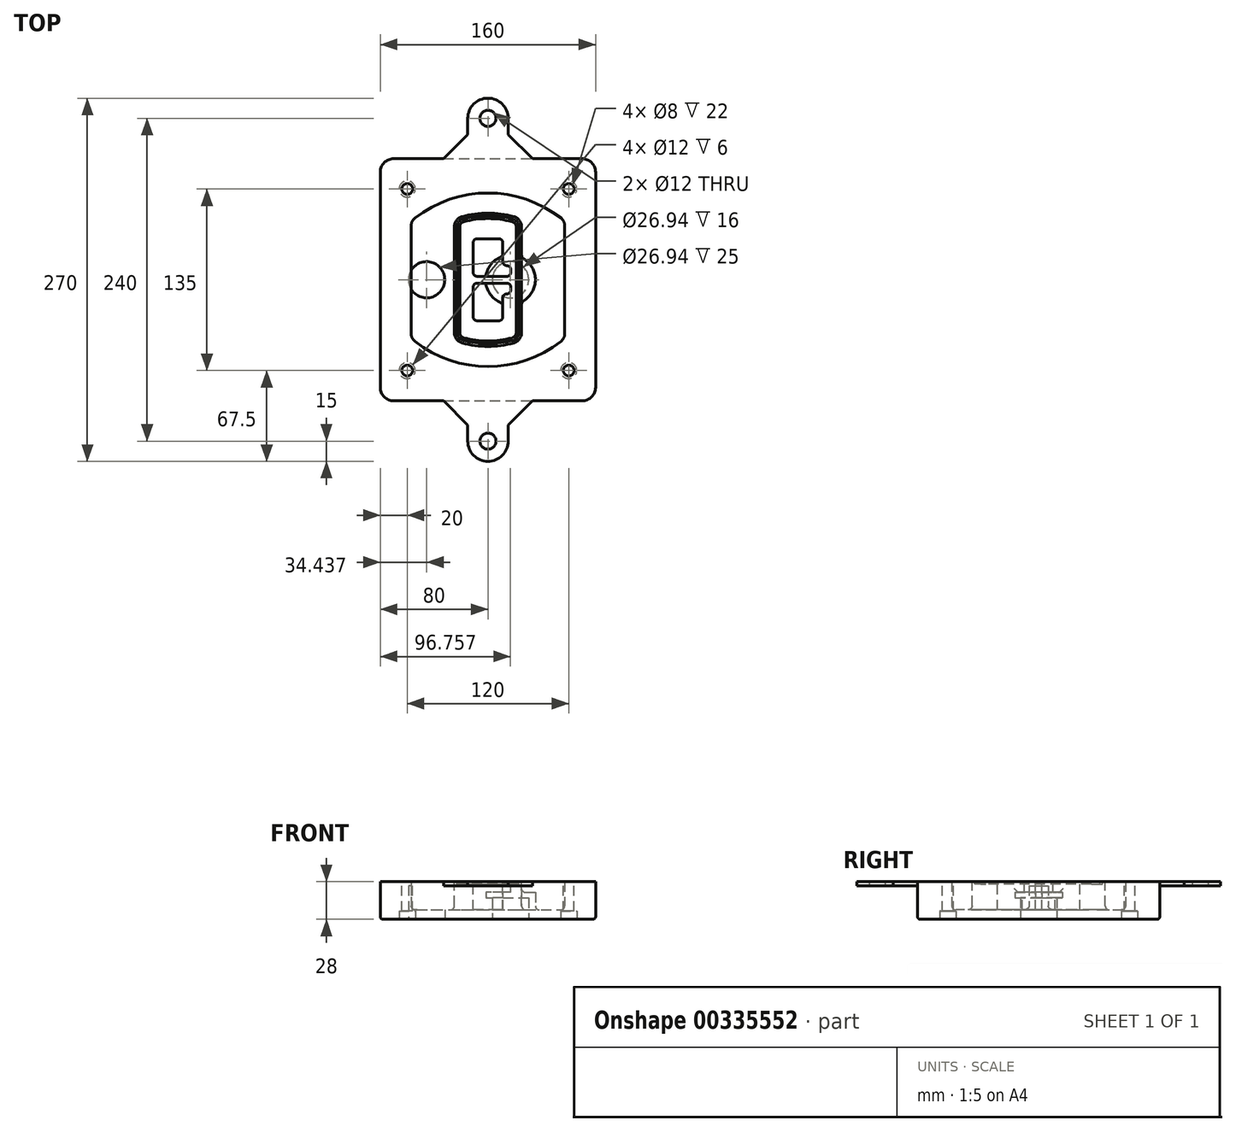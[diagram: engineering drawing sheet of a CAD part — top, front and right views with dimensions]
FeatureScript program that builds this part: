
annotation { "Feature Type Name" : "Feature", "Feature Type Description" : "" }
export const myFeature = defineFeature(function(context is Context, id is Id, definition is map)
    precondition{}
    {
        {
            var Q0;
            Q0=qCreatedBy(makeId("Top.planeOp"),FACE);
            var sketch = newSketch(context, id + "F0", { "sketchPlane" : qUnion([Q0])});
            skPoint(sketch, "E0.rect.middle", {"position": v(0, 0) * mm});
            skLineSegment(sketch, "E1.bottom", {"start": v(-70, -90) * mm, "end": v(70, -90) * mm});
            skLineSegment(sketch, "E1.top", {"start": v(-70, 90) * mm, "end": v(70, 90) * mm});
            skLineSegment(sketch, "E1.left", {"start": v(-80, -80) * mm, "end": v(-80, 80) * mm});
            skLineSegment(sketch, "E1.right", {"start": v(80, -80) * mm, "end": v(80, 80) * mm});
            skLineSegment(sketch, "E2", {"start": v(-80, 90) * mm, "end": v(80, -90) * mm, "construction": true});
            skLineSegment(sketch, "E3", {"start": v(80, 90) * mm, "end": v(-80, -90) * mm, "construction": true});
            skCircle(sketch, "E4", {"center": v(-60, 67.5) * mm, "radius": 4 * mm});
            skCircle(sketch, "E5", {"center": v(60, 67.5) * mm, "radius": 4 * mm});
            skCircle(sketch, "E6", {"center": v(60, -67.5) * mm, "radius": 4 * mm});
            skCircle(sketch, "E7", {"center": v(-60, -67.5) * mm, "radius": 4 * mm});
            skLineSegment(sketch, "E8", {"start": v(-60, 67.5) * mm, "end": v(60, 67.5) * mm, "construction": true});
            skLineSegment(sketch, "E9", {"start": v(60, 67.5) * mm, "end": v(60, -67.5) * mm, "construction": true});
            skLineSegment(sketch, "E10", {"start": v(60, -67.5) * mm, "end": v(-60, -67.5) * mm, "construction": true});
            skLineSegment(sketch, "E11", {"start": v(-60, -67.5) * mm, "end": v(-60, 67.5) * mm, "construction": true});
            skLineSegment(sketch, "E12", {"start": v(-60, 40.3) * mm, "end": v(-60, -40.3) * mm});
            skLineSegment(sketch, "E13", {"start": v(60, 40.3) * mm, "end": v(60, -40.3) * mm});
            skArc(sketch, "E14", {"start": v(56.15, 48.18) * mm, "mid": v(0, 67.5) * mm, "end": v(-56.15, 48.18) * mm});
            skArc(sketch, "E15", {"start": v(-56.15, -48.18) * mm, "mid": v(0, -67.5) * mm, "end": v(56.15, -48.18) * mm});
            skLineSegment(sketch, "E16", {"start": v(-60, 0) * mm, "end": v(60, 0) * mm, "construction": true});
            skPoint(sketch, "E17.visualSharp", {"position": v(-60, -45) * mm});
            skArc(sketch, "E17.filletArc", {"start": v(-60, -40.3) * mm, "mid": v(-58.99, -44.68) * mm, "end": v(-56.15, -48.18) * mm});
            skPoint(sketch, "E18.visualSharp", {"position": v(-60, 45) * mm});
            skArc(sketch, "E18.filletArc", {"start": v(-56.15, 48.18) * mm, "mid": v(-58.99, 44.68) * mm, "end": v(-60, 40.3) * mm});
            skPoint(sketch, "E19.visualSharp", {"position": v(60, 45) * mm});
            skArc(sketch, "E19.filletArc", {"start": v(60, 40.3) * mm, "mid": v(58.99, 44.68) * mm, "end": v(56.15, 48.18) * mm});
            skPoint(sketch, "E20.visualSharp", {"position": v(60, -45) * mm});
            skArc(sketch, "E20.filletArc", {"start": v(56.15, -48.18) * mm, "mid": v(58.99, -44.68) * mm, "end": v(60, -40.3) * mm});
            skPoint(sketch, "E21.visualSharp", {"position": v(-80, 90) * mm});
            skArc(sketch, "E21.filletArc", {"start": v(-70, 90) * mm, "mid": v(-77.07, 87.07) * mm, "end": v(-80, 80) * mm});
            skPoint(sketch, "E22.visualSharp", {"position": v(80, 90) * mm});
            skArc(sketch, "E22.filletArc", {"start": v(80, 80) * mm, "mid": v(77.07, 87.07) * mm, "end": v(70, 90) * mm});
            skPoint(sketch, "E23.visualSharp", {"position": v(80, -90) * mm});
            skArc(sketch, "E23.filletArc", {"start": v(70, -90) * mm, "mid": v(77.07, -87.07) * mm, "end": v(80, -80) * mm});
            skPoint(sketch, "E24.visualSharp", {"position": v(-80, -90) * mm});
            skArc(sketch, "E24.filletArc", {"start": v(-80, -80) * mm, "mid": v(-77.07, -87.07) * mm, "end": v(-70, -90) * mm});
            skArc(sketch, "E25.0", {"start": v(57, 40.3) * mm, "mid": v(56.3, 43.36) * mm, "end": v(54.3, 45.81) * mm});
            skLineSegment(sketch, "E25.1", {"start": v(57, 40.3) * mm, "end": v(57, -40.3) * mm});
            skArc(sketch, "E25.2", {"start": v(54.3, -45.81) * mm, "mid": v(56.3, -43.36) * mm, "end": v(57, -40.3) * mm});
            skArc(sketch, "E25.3", {"start": v(-54.3, -45.81) * mm, "mid": v(0, -64.5) * mm, "end": v(54.3, -45.81) * mm});
            skArc(sketch, "E25.4", {"start": v(-57, -40.3) * mm, "mid": v(-56.3, -43.36) * mm, "end": v(-54.3, -45.81) * mm});
            skArc(sketch, "E25.5", {"start": v(54.3, 45.81) * mm, "mid": v(0, 64.5) * mm, "end": v(-54.3, 45.81) * mm});
            skLineSegment(sketch, "E25.6", {"start": v(-57, 40.3) * mm, "end": v(-57, -40.3) * mm});
            skArc(sketch, "E25.7", {"start": v(-54.3, 45.81) * mm, "mid": v(-56.3, 43.36) * mm, "end": v(-57, 40.3) * mm});
            skArc(sketch, "E26.0", {"start": v(-58.62, 51.33) * mm, "mid": v(-62.58, 46.43) * mm, "end": v(-64, 40.3) * mm});
            skArc(sketch, "E26.1", {"start": v(58.62, 51.33) * mm, "mid": v(0, 71.5) * mm, "end": v(-58.62, 51.33) * mm});
            skArc(sketch, "E26.2", {"start": v(64, 40.3) * mm, "mid": v(62.58, 46.43) * mm, "end": v(58.62, 51.33) * mm});
            skLineSegment(sketch, "E26.3", {"start": v(64, 40.3) * mm, "end": v(64, -40.3) * mm});
            skArc(sketch, "E26.4", {"start": v(58.62, -51.33) * mm, "mid": v(62.58, -46.43) * mm, "end": v(64, -40.3) * mm});
            skLineSegment(sketch, "E26.5", {"start": v(-64, 40.3) * mm, "end": v(-64, -40.3) * mm});
            skArc(sketch, "E26.6", {"start": v(-58.62, -51.33) * mm, "mid": v(0, -71.5) * mm, "end": v(58.62, -51.33) * mm});
            skArc(sketch, "E26.7", {"start": v(-64, -40.3) * mm, "mid": v(-62.58, -46.43) * mm, "end": v(-58.62, -51.33) * mm});
            skSolve(sketch);
        }
        {
            var Q0;
            Q0=makeQuery(id+"F0.imprint","IMPRINT",FACE,{"disambiguationData":[TD([[makeQuery(id+"F0.imprint","IMPRINT",EDGE,{"derivedFrom":sQuery(id+"F0.wireOp",EDGE,"E1.bottom")}),1.0]])]});
            var Q1;
            Q1=makeQuery(id+"F0.imprint","IMPRINT",FACE,{"disambiguationData":[TD([[makeQuery(id+"F0.imprint","IMPRINT",EDGE,{"derivedFrom":sQuery(id+"F0.wireOp",EDGE,"E12")}),1.0]])]});
            var Q2;
            Q2=makeQuery(id+"F0.imprint","IMPRINT",FACE,{"disambiguationData":[TD([[makeQuery(id+"F0.imprint","IMPRINT",EDGE,{"derivedFrom":sQuery(id+"F0.wireOp",EDGE,"E25.0")}),1.0]])]});
            var Q3;
            Q3=makeQuery(id+"F0.imprint","IMPRINT",FACE,{"disambiguationData":[TD([[makeQuery(id+"F0.imprint","IMPRINT",EDGE,{"derivedFrom":sQuery(id+"F0.wireOp",EDGE,"E12")}),-1.0]])]});
            extrude(context, id + "F1", {"entities" : qUnion([Q0, Q1, Q2, Q3]), "oppositeDirection" : true, "depth" : 25 * mm});
        }
        {
            var Q0;
            Q0=makeQuery(id+"F0.imprint","IMPRINT",FACE,{"disambiguationData":[TD([[makeQuery(id+"F0.imprint","IMPRINT",EDGE,{"derivedFrom":sQuery(id+"F0.wireOp",EDGE,"E12")}),1.0]])]});
            extrude(context, id + "F2", {"entities" : qUnion([Q0]), "operationType" : NewBodyOperationType.ADD, "depth" : 3 * mm});
        }
        {
            var Q0;
            Q0=makeQuery(id+"F0.imprint","IMPRINT",FACE,{"disambiguationData":[TD([[makeQuery(id+"F0.imprint","IMPRINT",EDGE,{"derivedFrom":sQuery(id+"F0.wireOp",EDGE,"E25.0")}),1.0]])]});
            extrude(context, id + "F3", {"entities" : qUnion([Q0]), "operationType" : NewBodyOperationType.REMOVE, "oppositeDirection" : true, "depth" : 18 * mm});
        }
        {
            var Q0;
            Q0=makeQuery(id+"F2.opExtrude","CAP_FACE",FACE,{"disambiguationData":[OSD([sQuery(id+"F0.wireOp",EDGE,"E12"),sQuery(id+"F0.wireOp",EDGE,"E13"),sQuery(id+"F0.wireOp",EDGE,"E14"),sQuery(id+"F0.wireOp",EDGE,"E15"),sQuery(id+"F0.wireOp",EDGE,"E17.filletArc"),sQuery(id+"F0.wireOp",EDGE,"E18.filletArc"),sQuery(id+"F0.wireOp",EDGE,"E19.filletArc"),sQuery(id+"F0.wireOp",EDGE,"E20.filletArc"),sQuery(id+"F0.wireOp",EDGE,"E25.0"),sQuery(id+"F0.wireOp",EDGE,"E25.1"),sQuery(id+"F0.wireOp",EDGE,"E25.2"),sQuery(id+"F0.wireOp",EDGE,"E25.3"),sQuery(id+"F0.wireOp",EDGE,"E25.4"),sQuery(id+"F0.wireOp",EDGE,"E25.5"),sQuery(id+"F0.wireOp",EDGE,"E25.6"),sQuery(id+"F0.wireOp",EDGE,"E25.7")])],"isStart":false});
            var sketch = newSketch(context, id + "F4", { "sketchPlane" : qUnion([Q0])});
            skArc(sketch, "E27.0", {"start": v(-19.08, -46.97) * mm, "mid": v(0, -49.5) * mm, "end": v(19.08, -46.97) * mm});
            skArc(sketch, "E28.0", {"start": v(19.08, 46.97) * mm, "mid": v(0, 49.5) * mm, "end": v(-19.08, 46.97) * mm});
            skLineSegment(sketch, "E29", {"start": v(-25, 39.25) * mm, "end": v(-25, -39.25) * mm});
            skLineSegment(sketch, "E30", {"start": v(25, 39.25) * mm, "end": v(25, -39.25) * mm});
            skLineSegment(sketch, "E31", {"start": v(-25, 45.1) * mm, "end": v(25, 45.1) * mm, "construction": true});
            skLineSegment(sketch, "E32", {"start": v(-25, -45.1) * mm, "end": v(25, -45.1) * mm, "construction": true});
            skPoint(sketch, "E33.visualSharp", {"position": v(-25, 45.1) * mm});
            skArc(sketch, "E33.filletArc", {"start": v(-19.08, 46.97) * mm, "mid": v(-23.35, 44.11) * mm, "end": v(-25, 39.25) * mm});
            skPoint(sketch, "E34.visualSharp", {"position": v(25, 45.1) * mm});
            skArc(sketch, "E34.filletArc", {"start": v(25, 39.25) * mm, "mid": v(23.35, 44.11) * mm, "end": v(19.08, 46.97) * mm});
            skPoint(sketch, "E35.visualSharp", {"position": v(25, -45.1) * mm});
            skArc(sketch, "E35.filletArc", {"start": v(19.08, -46.97) * mm, "mid": v(23.35, -44.11) * mm, "end": v(25, -39.25) * mm});
            skPoint(sketch, "E36.visualSharp", {"position": v(-25, -45.1) * mm});
            skArc(sketch, "E36.filletArc", {"start": v(-25, -39.25) * mm, "mid": v(-23.35, -44.11) * mm, "end": v(-19.08, -46.97) * mm});
            skArc(sketch, "E37.0", {"start": v(54.3, 45.81) * mm, "mid": v(0, 64.5) * mm, "end": v(-54.3, 45.81) * mm});
            skArc(sketch, "E37.1", {"start": v(-54.3, 45.81) * mm, "mid": v(-56.3, 43.36) * mm, "end": v(-57, 40.3) * mm});
            skLineSegment(sketch, "E37.2", {"start": v(-57, 40.3) * mm, "end": v(-57, -40.3) * mm});
            skArc(sketch, "E37.3", {"start": v(-57, -40.3) * mm, "mid": v(-56.3, -43.36) * mm, "end": v(-54.3, -45.81) * mm});
            skArc(sketch, "E37.4", {"start": v(-54.3, -45.81) * mm, "mid": v(0, -64.5) * mm, "end": v(54.3, -45.81) * mm});
            skArc(sketch, "E37.5", {"start": v(54.3, -45.81) * mm, "mid": v(56.3, -43.36) * mm, "end": v(57, -40.3) * mm});
            skLineSegment(sketch, "E37.6", {"start": v(57, 40.3) * mm, "end": v(57, -40.3) * mm});
            skArc(sketch, "E37.7", {"start": v(57, 40.3) * mm, "mid": v(56.3, 43.36) * mm, "end": v(54.3, 45.81) * mm});
            skLineSegment(sketch, "E38.0", {"start": v(23, 39.25) * mm, "end": v(23, -39.25) * mm});
            skArc(sketch, "E38.1", {"start": v(18.56, -45.04) * mm, "mid": v(21.76, -42.9) * mm, "end": v(23, -39.25) * mm});
            skArc(sketch, "E38.2", {"start": v(-18.56, -45.04) * mm, "mid": v(0, -47.5) * mm, "end": v(18.56, -45.04) * mm});
            skArc(sketch, "E38.3", {"start": v(-23, -39.25) * mm, "mid": v(-21.76, -42.9) * mm, "end": v(-18.56, -45.04) * mm});
            skLineSegment(sketch, "E38.4", {"start": v(-23, 39.25) * mm, "end": v(-23, -39.25) * mm});
            skArc(sketch, "E38.5", {"start": v(23, 39.25) * mm, "mid": v(21.76, 42.9) * mm, "end": v(18.56, 45.04) * mm});
            skArc(sketch, "E38.6", {"start": v(-18.56, 45.04) * mm, "mid": v(-21.76, 42.9) * mm, "end": v(-23, 39.25) * mm});
            skArc(sketch, "E38.7", {"start": v(18.56, 45.04) * mm, "mid": v(0, 47.5) * mm, "end": v(-18.56, 45.04) * mm});
            skArc(sketch, "E39.0", {"start": v(21, 39.25) * mm, "mid": v(20.18, 41.68) * mm, "end": v(18.04, 43.1) * mm});
            skLineSegment(sketch, "E39.1", {"start": v(21, 39.25) * mm, "end": v(21, -39.25) * mm});
            skArc(sketch, "E39.2", {"start": v(18.04, -43.1) * mm, "mid": v(20.18, -41.68) * mm, "end": v(21, -39.25) * mm});
            skArc(sketch, "E39.3", {"start": v(-18.04, -43.1) * mm, "mid": v(0, -45.5) * mm, "end": v(18.04, -43.1) * mm});
            skArc(sketch, "E39.4", {"start": v(-21, -39.25) * mm, "mid": v(-20.18, -41.68) * mm, "end": v(-18.04, -43.1) * mm});
            skArc(sketch, "E39.5", {"start": v(18.04, 43.1) * mm, "mid": v(0, 45.5) * mm, "end": v(-18.04, 43.1) * mm});
            skLineSegment(sketch, "E39.6", {"start": v(-21, 39.25) * mm, "end": v(-21, -39.25) * mm});
            skArc(sketch, "E39.7", {"start": v(-18.04, 43.1) * mm, "mid": v(-20.18, 41.68) * mm, "end": v(-21, 39.25) * mm});
            skLineSegment(sketch, "E40", {"start": v(-25, 0) * mm, "end": v(25, 0) * mm, "construction": true});
            skLineSegment(sketch, "E41", {"start": v(-11, 5.5) * mm, "end": v(-11, 27.5) * mm});
            skLineSegment(sketch, "E42", {"start": v(-8, 30.5) * mm, "end": v(8, 30.5) * mm});
            skLineSegment(sketch, "E43", {"start": v(11, 27.5) * mm, "end": v(11, 13.5) * mm});
            skLineSegment(sketch, "E44", {"start": v(14, 10.5) * mm, "end": v(14, 10.5) * mm});
            skLineSegment(sketch, "E45", {"start": v(17, 7.5) * mm, "end": v(17, 5.5) * mm});
            skLineSegment(sketch, "E46", {"start": v(14, 2.5) * mm, "end": v(-8, 2.5) * mm});
            skPoint(sketch, "E47.visualSharp", {"position": v(-11, 30.5) * mm});
            skArc(sketch, "E47.filletArc", {"start": v(-8, 30.5) * mm, "mid": v(-10.12, 29.62) * mm, "end": v(-11, 27.5) * mm});
            skPoint(sketch, "E48.visualSharp", {"position": v(11, 30.5) * mm});
            skArc(sketch, "E48.filletArc", {"start": v(11, 27.5) * mm, "mid": v(10.12, 29.62) * mm, "end": v(8, 30.5) * mm});
            skPoint(sketch, "E49.visualSharp", {"position": v(11, 10.5) * mm});
            skArc(sketch, "E49.filletArc", {"start": v(11, 13.5) * mm, "mid": v(11.88, 11.38) * mm, "end": v(14, 10.5) * mm});
            skPoint(sketch, "E50.visualSharp", {"position": v(17, 10.5) * mm});
            skArc(sketch, "E50.filletArc", {"start": v(17, 7.5) * mm, "mid": v(16.12, 9.62) * mm, "end": v(14, 10.5) * mm});
            skPoint(sketch, "E51.visualSharp", {"position": v(17, 2.5) * mm});
            skArc(sketch, "E51.filletArc", {"start": v(14, 2.5) * mm, "mid": v(16.12, 3.38) * mm, "end": v(17, 5.5) * mm});
            skPoint(sketch, "E52.visualSharp", {"position": v(-11, 2.5) * mm});
            skArc(sketch, "E52.filletArc", {"start": v(-11, 5.5) * mm, "mid": v(-10.12, 3.38) * mm, "end": v(-8, 2.5) * mm});
            skLineSegment(sketch, "E53.0.MirrorCS", {"start": v(14, -2.5) * mm, "end": v(-8, -2.5) * mm});
            skArc(sketch, "E54.0.MirrorCS", {"start": v(-11, -5.5) * mm, "mid": v(-10.12, -3.38) * mm, "end": v(-8, -2.5) * mm});
            skLineSegment(sketch, "E55.0.MirrorCS", {"start": v(-11, -5.5) * mm, "end": v(-11, -27.5) * mm});
            skArc(sketch, "E56.0.MirrorCS", {"start": v(-8, -30.5) * mm, "mid": v(-10.12, -29.62) * mm, "end": v(-11, -27.5) * mm});
            skLineSegment(sketch, "E57.0.MirrorCS", {"start": v(-8, -30.5) * mm, "end": v(8, -30.5) * mm});
            skArc(sketch, "E58.0.MirrorCS", {"start": v(11, -27.5) * mm, "mid": v(10.12, -29.62) * mm, "end": v(8, -30.5) * mm});
            skLineSegment(sketch, "E59.0.MirrorCS", {"start": v(11, -27.5) * mm, "end": v(11, -13.5) * mm});
            skArc(sketch, "E60.0.MirrorCS", {"start": v(11, -13.5) * mm, "mid": v(11.88, -11.38) * mm, "end": v(14, -10.5) * mm});
            skArc(sketch, "E61.0.MirrorCS", {"start": v(17, -7.5) * mm, "mid": v(16.12, -9.62) * mm, "end": v(14, -10.5) * mm});
            skLineSegment(sketch, "E62.0.MirrorCS", {"start": v(17, -7.5) * mm, "end": v(17, -5.5) * mm});
            skArc(sketch, "E63.0.MirrorCS", {"start": v(14, -2.5) * mm, "mid": v(16.12, -3.38) * mm, "end": v(17, -5.5) * mm});
            skSolve(sketch);
        }
        {
            var Q0;
            Q0=makeQuery(id+"F4.imprint","IMPRINT",FACE,{"disambiguationData":[TD([[makeQuery(id+"F4.imprint","IMPRINT",EDGE,{"derivedFrom":sQuery(id+"F4.wireOp",EDGE,"E27.0")}),1.0]])]});
            var Q1;
            Q1=makeQuery(id+"F4.imprint","IMPRINT",FACE,{"disambiguationData":[TD([[makeQuery(id+"F4.imprint","IMPRINT",EDGE,{"derivedFrom":sQuery(id+"F4.wireOp",EDGE,"E38.0")}),-1.0]])]});
            var Q2;
            Q2=makeQuery(id+"F4.imprint","IMPRINT",FACE,{"disambiguationData":[TD([[makeQuery(id+"F4.imprint","IMPRINT",EDGE,{"derivedFrom":sQuery(id+"F4.wireOp",EDGE,"E39.0")}),1.0]])]});
            extrude(context, id + "F5", {"entities" : qUnion([Q0, Q1, Q2]), "operationType" : NewBodyOperationType.ADD, "endBound" : BoundingType.UP_TO_NEXT, "oppositeDirection" : true, "depth" : 25 * mm});
        }
        {
            var Q0;
            Q0=makeQuery(id+"F4.imprint","IMPRINT",FACE,{"disambiguationData":[TD([[makeQuery(id+"F4.imprint","IMPRINT",EDGE,{"derivedFrom":sQuery(id+"F4.wireOp",EDGE,"E38.0")}),-1.0]])]});
            extrude(context, id + "F6", {"entities" : qUnion([Q0]), "operationType" : NewBodyOperationType.REMOVE, "oppositeDirection" : true, "depth" : 2 * mm});
        }
        {
            var Q0;
            Q0=makeQuery(id+"F1.opExtrude","CAP_FACE",FACE,{"disambiguationData":[OSD([sQuery(id+"F0.wireOp",EDGE,"E1.bottom"),sQuery(id+"F0.wireOp",EDGE,"E1.top"),sQuery(id+"F0.wireOp",EDGE,"E1.left"),sQuery(id+"F0.wireOp",EDGE,"E1.right"),sQuery(id+"F0.wireOp",EDGE,"E4"),sQuery(id+"F0.wireOp",EDGE,"E5"),sQuery(id+"F0.wireOp",EDGE,"E6"),sQuery(id+"F0.wireOp",EDGE,"E7"),sQuery(id+"F0.wireOp",EDGE,"E21.filletArc"),sQuery(id+"F0.wireOp",EDGE,"E22.filletArc"),sQuery(id+"F0.wireOp",EDGE,"E23.filletArc"),sQuery(id+"F0.wireOp",EDGE,"E24.filletArc")])],"isStart":false});
            var sketch = newSketch(context, id + "F7", { "sketchPlane" : qUnion([Q0])});
            skCircle(sketch, "E64", {"center": v(16.76, 0) * mm, "radius": 13.47 * mm});
            skCircle(sketch, "E65", {"center": v(-45.56, 0) * mm, "radius": 13.47 * mm});
            skLineSegment(sketch, "E66", {"start": v(80, 0) * mm, "end": v(-80, 0) * mm});
            skCircle(sketch, "E67", {"center": v(16.76, 0) * mm, "radius": 18.47 * mm});
            skCircle(sketch, "E68", {"center": v(60, -67.5) * mm, "radius": 6 * mm});
            skCircle(sketch, "E69", {"center": v(-60, -67.5) * mm, "radius": 6 * mm});
            skCircle(sketch, "E70", {"center": v(-60, 67.5) * mm, "radius": 6 * mm});
            skCircle(sketch, "E71", {"center": v(60, 67.5) * mm, "radius": 6 * mm});
            skSolve(sketch);
        }
        {
            var Q0;
            {var subQ1=sQuery(id+"F7.wireOp",EDGE,"E66");var subQ4=sQuery(id+"F7.wireOp",EDGE,"E64");var subQ6=makeQuery(id+"F7.imprint","INTERSECT",VERTEX,{"disambiguationData":[OD(0.0)],"derivedFrom":[subQ4,subQ1]});Q0=makeQuery(id+"F7.imprint","IMPRINT",FACE,{"disambiguationData":[TD([[makeQuery(id+"F7.imprint","IMPRINT",EDGE,{"disambiguationData":[TD([[subQ6,-1.0]])],"derivedFrom":subQ4}),-1.0]])]});}
            var Q1;
            {var subQ0=sQuery(id+"F7.wireOp",EDGE,"E66");var subQ1=sQuery(id+"F7.wireOp",EDGE,"E64");var subQ3=makeQuery(id+"F7.imprint","INTERSECT",VERTEX,{"disambiguationData":[OD(0.0)],"derivedFrom":[subQ1,subQ0]});Q1=makeQuery(id+"F7.imprint","IMPRINT",FACE,{"disambiguationData":[TD([[makeQuery(id+"F7.imprint","IMPRINT",EDGE,{"disambiguationData":[TD([[subQ3,-1.0]])],"derivedFrom":subQ1}),1.0]])]});}
            var Q2;
            {var subQ0=sQuery(id+"F7.wireOp",EDGE,"E66");var subQ1=sQuery(id+"F7.wireOp",EDGE,"E64");var subQ3=makeQuery(id+"F7.imprint","INTERSECT",VERTEX,{"disambiguationData":[OD(0.0)],"derivedFrom":[subQ1,subQ0]});Q2=makeQuery(id+"F7.imprint","IMPRINT",FACE,{"disambiguationData":[TD([[makeQuery(id+"F7.imprint","IMPRINT",EDGE,{"disambiguationData":[TD([[subQ3,1.0]])],"derivedFrom":subQ1}),1.0]])]});}
            var Q3;
            {var subQ1=sQuery(id+"F7.wireOp",EDGE,"E66");var subQ4=sQuery(id+"F7.wireOp",EDGE,"E64");var subQ6=makeQuery(id+"F7.imprint","INTERSECT",VERTEX,{"disambiguationData":[OD(0.0)],"derivedFrom":[subQ4,subQ1]});Q3=makeQuery(id+"F7.imprint","IMPRINT",FACE,{"disambiguationData":[TD([[makeQuery(id+"F7.imprint","IMPRINT",EDGE,{"disambiguationData":[TD([[subQ6,1.0]])],"derivedFrom":subQ4}),-1.0]])]});}
            extrude(context, id + "F8", {"entities" : qUnion([Q0, Q1, Q2, Q3]), "operationType" : NewBodyOperationType.ADD, "oppositeDirection" : true, "depth" : 20 * mm});
        }
        {
            var Q0;
            {var subQ0=sQuery(id+"F7.wireOp",EDGE,"E66");var subQ1=sQuery(id+"F7.wireOp",EDGE,"E64");var subQ3=makeQuery(id+"F7.imprint","INTERSECT",VERTEX,{"disambiguationData":[OD(0.0)],"derivedFrom":[subQ1,subQ0]});Q0=makeQuery(id+"F7.imprint","IMPRINT",FACE,{"disambiguationData":[TD([[makeQuery(id+"F7.imprint","IMPRINT",EDGE,{"disambiguationData":[TD([[subQ3,-1.0]])],"derivedFrom":subQ1}),1.0]])]});}
            var Q1;
            {var subQ0=sQuery(id+"F7.wireOp",EDGE,"E66");var subQ1=sQuery(id+"F7.wireOp",EDGE,"E64");var subQ3=makeQuery(id+"F7.imprint","INTERSECT",VERTEX,{"disambiguationData":[OD(0.0)],"derivedFrom":[subQ1,subQ0]});Q1=makeQuery(id+"F7.imprint","IMPRINT",FACE,{"disambiguationData":[TD([[makeQuery(id+"F7.imprint","IMPRINT",EDGE,{"disambiguationData":[TD([[subQ3,1.0]])],"derivedFrom":subQ1}),1.0]])]});}
            extrude(context, id + "F9", {"entities" : qUnion([Q0, Q1]), "operationType" : NewBodyOperationType.REMOVE, "oppositeDirection" : true, "depth" : 16 * mm});
        }
        {
            var Q0;
            {var subQ0=sQuery(id+"F7.wireOp",EDGE,"E66");var subQ1=sQuery(id+"F7.wireOp",EDGE,"E65");var subQ3=makeQuery(id+"F7.imprint","INTERSECT",VERTEX,{"disambiguationData":[OD(0.0)],"derivedFrom":[subQ1,subQ0]});Q0=makeQuery(id+"F7.imprint","IMPRINT",FACE,{"disambiguationData":[TD([[makeQuery(id+"F7.imprint","IMPRINT",EDGE,{"disambiguationData":[TD([[subQ3,-1.0]])],"derivedFrom":subQ1}),1.0]])]});}
            var Q1;
            {var subQ0=sQuery(id+"F7.wireOp",EDGE,"E66");var subQ1=sQuery(id+"F7.wireOp",EDGE,"E65");var subQ3=makeQuery(id+"F7.imprint","INTERSECT",VERTEX,{"disambiguationData":[OD(0.0)],"derivedFrom":[subQ1,subQ0]});Q1=makeQuery(id+"F7.imprint","IMPRINT",FACE,{"disambiguationData":[TD([[makeQuery(id+"F7.imprint","IMPRINT",EDGE,{"disambiguationData":[TD([[subQ3,1.0]])],"derivedFrom":subQ1}),1.0]])]});}
            extrude(context, id + "F10", {"entities" : qUnion([Q0, Q1]), "operationType" : NewBodyOperationType.REMOVE, "oppositeDirection" : true, "depth" : 25 * mm});
        }
        {
            var Q0;
            Q0=makeQuery(id+"F7.imprint","IMPRINT",FACE,{"disambiguationData":[TD([[makeQuery(id+"F7.imprint","IMPRINT",EDGE,{"derivedFrom":sQuery(id+"F7.wireOp",EDGE,"E68")}),1.0]])]});
            var Q1;
            Q1=makeQuery(id+"F7.imprint","IMPRINT",FACE,{"disambiguationData":[TD([[makeQuery(id+"F7.imprint","IMPRINT",EDGE,{"derivedFrom":makeQuery(id+"F1.opExtrude","CAP_EDGE",EDGE,{"disambiguationData":[OSD([sQuery(id+"F0.wireOp",EDGE,"E5")])],"isStart":false})}),-1.0]])]});
            var Q2;
            Q2=makeQuery(id+"F7.imprint","IMPRINT",FACE,{"disambiguationData":[TD([[makeQuery(id+"F7.imprint","IMPRINT",EDGE,{"derivedFrom":sQuery(id+"F7.wireOp",EDGE,"E69")}),1.0]])]});
            var Q3;
            Q3=makeQuery(id+"F7.imprint","IMPRINT",FACE,{"disambiguationData":[TD([[makeQuery(id+"F7.imprint","IMPRINT",EDGE,{"derivedFrom":makeQuery(id+"F1.opExtrude","CAP_EDGE",EDGE,{"disambiguationData":[OSD([sQuery(id+"F0.wireOp",EDGE,"E4")])],"isStart":false})}),-1.0]])]});
            var Q4;
            Q4=makeQuery(id+"F7.imprint","IMPRINT",FACE,{"disambiguationData":[TD([[makeQuery(id+"F7.imprint","IMPRINT",EDGE,{"derivedFrom":sQuery(id+"F7.wireOp",EDGE,"E70")}),1.0]])]});
            var Q5;
            Q5=makeQuery(id+"F7.imprint","IMPRINT",FACE,{"disambiguationData":[TD([[makeQuery(id+"F7.imprint","IMPRINT",EDGE,{"derivedFrom":makeQuery(id+"F1.opExtrude","CAP_EDGE",EDGE,{"disambiguationData":[OSD([sQuery(id+"F0.wireOp",EDGE,"E7")])],"isStart":false})}),-1.0]])]});
            var Q6;
            Q6=makeQuery(id+"F7.imprint","IMPRINT",FACE,{"disambiguationData":[TD([[makeQuery(id+"F7.imprint","IMPRINT",EDGE,{"derivedFrom":sQuery(id+"F7.wireOp",EDGE,"E71")}),1.0]])]});
            var Q7;
            Q7=makeQuery(id+"F7.imprint","IMPRINT",FACE,{"disambiguationData":[TD([[makeQuery(id+"F7.imprint","IMPRINT",EDGE,{"derivedFrom":makeQuery(id+"F1.opExtrude","CAP_EDGE",EDGE,{"disambiguationData":[OSD([sQuery(id+"F0.wireOp",EDGE,"E6")])],"isStart":false})}),-1.0]])]});
            extrude(context, id + "F11", {"entities" : qUnion([Q0, Q1, Q2, Q3, Q4, Q5, Q6, Q7]), "operationType" : NewBodyOperationType.REMOVE, "oppositeDirection" : true, "depth" : 6 * mm});
        }
        {
            var Q0;
            Q0=makeQuery(id+"F9.boolean.opBoolean","COPY",FACE,{"derivedFrom":makeQuery(id+"F9.opExtrude","CAP_FACE",FACE,{"disambiguationData":[OSD([sQuery(id+"F7.wireOp",EDGE,"E64")])],"isStart":false})});
            var sketch = newSketch(context, id + "F12", { "sketchPlane" : qUnion([Q0])});
            skArc(sketch, "E72.0", {"start": v(11, 17.55) * mm, "mid": v(2.57, 11.82) * mm, "end": v(-1.54, 2.5) * mm});
            skArc(sketch, "E72.1", {"start": v(-1.54, -2.5) * mm, "mid": v(2.57, -11.82) * mm, "end": v(11, -17.55) * mm});
            skLineSegment(sketch, "E73", {"start": v(-1.54, -2.5) * mm, "end": v(14, -2.5) * mm});
            skLineSegment(sketch, "E74.0", {"start": v(14, 2.5) * mm, "end": v(-1.54, 2.5) * mm});
            skArc(sketch, "E74.1", {"start": v(14, 2.5) * mm, "mid": v(16.12, 3.38) * mm, "end": v(17, 5.5) * mm});
            skLineSegment(sketch, "E74.2", {"start": v(17, 7.5) * mm, "end": v(17, 5.5) * mm});
            skArc(sketch, "E74.3", {"start": v(17, 7.5) * mm, "mid": v(16.12, 9.62) * mm, "end": v(14, 10.5) * mm});
            skArc(sketch, "E74.4", {"start": v(11, 13.5) * mm, "mid": v(11.88, 11.38) * mm, "end": v(14, 10.5) * mm});
            skLineSegment(sketch, "E74.5", {"start": v(11, 17.55) * mm, "end": v(11, 13.5) * mm});
            skLineSegment(sketch, "E74.7", {"start": v(14, -2.5) * mm, "end": v(-1.54, -2.5) * mm});
            skArc(sketch, "E74.8", {"start": v(14, -2.5) * mm, "mid": v(16.12, -3.38) * mm, "end": v(17, -5.5) * mm});
            skLineSegment(sketch, "E74.9", {"start": v(17, -7.5) * mm, "end": v(17, -5.5) * mm});
            skArc(sketch, "E74.10", {"start": v(17, -7.5) * mm, "mid": v(16.12, -9.62) * mm, "end": v(14, -10.5) * mm});
            skArc(sketch, "E74.11", {"start": v(11, -13.5) * mm, "mid": v(11.88, -11.38) * mm, "end": v(14, -10.5) * mm});
            skLineSegment(sketch, "E74.12", {"start": v(11, -17.55) * mm, "end": v(11, -13.5) * mm});
            skPoint(sketch, "E75.orphan", {"position": v(11, -27.5) * mm});
            skPoint(sketch, "E76.orphan", {"position": v(-8, -2.5) * mm});
            skPoint(sketch, "E77.orphan", {"position": v(-8, 2.5) * mm});
            skPoint(sketch, "E78.orphan", {"position": v(11, 27.5) * mm});
            skSolve(sketch);
        }
        {
            var Q0;
            {var subQ7=sQuery(id+"F12.wireOp",EDGE,"E72.0");var subQ14=sQuery(id+"F12.wireOp",EDGE,"E72.1");var subQ16=sQuery(id+"F12.wireOp",EDGE,"E74.1");var subQ18=sQuery(id+"F12.wireOp",EDGE,"E74.8");Q0=qUnion([makeQuery(id+"F12.imprint","IMPRINT",FACE,{"disambiguationData":[TD([[makeQuery(id+"F12.imprint","IMPRINT",EDGE,{"derivedFrom":subQ7}),1.0]])]}),makeQuery(id+"F12.imprint","IMPRINT",FACE,{"disambiguationData":[TD([[makeQuery(id+"F12.imprint","IMPRINT",EDGE,{"derivedFrom":subQ14}),1.0]])]}),makeQuery(id+"F12.imprint","IMPRINT",FACE,{"disambiguationData":[TD([[makeQuery(id+"F12.imprint","IMPRINT",EDGE,{"derivedFrom":subQ16}),1.0]])]}),makeQuery(id+"F12.imprint","IMPRINT",FACE,{"disambiguationData":[TD([[makeQuery(id+"F12.imprint","IMPRINT",EDGE,{"derivedFrom":subQ18}),-1.0]])]})]);}
            var Q1;
            Q1=makeQuery(id+"F5.boolean.opBoolean","SPLIT",FACE,{"disambiguationData":[TD([makeQuery(id+"F5.opExtrude","SWEPT_FACE",FACE,{"disambiguationData":[OSD([sQuery(id+"F4.wireOp",EDGE,"E41")])]})])],"derivedFrom":makeQuery(id+"F3.boolean.opBoolean","COPY",FACE,{"derivedFrom":makeQuery(id+"F3.opExtrude","CAP_FACE",FACE,{"disambiguationData":[OSD([sQuery(id+"F0.wireOp",EDGE,"E25.0"),sQuery(id+"F0.wireOp",EDGE,"E25.1"),sQuery(id+"F0.wireOp",EDGE,"E25.2"),sQuery(id+"F0.wireOp",EDGE,"E25.3"),sQuery(id+"F0.wireOp",EDGE,"E25.4"),sQuery(id+"F0.wireOp",EDGE,"E25.5"),sQuery(id+"F0.wireOp",EDGE,"E25.6"),sQuery(id+"F0.wireOp",EDGE,"E25.7")])],"isStart":false})})});
            extrude(context, id + "F13", {"entities" : qUnion([Q0]), "operationType" : NewBodyOperationType.REMOVE, "endBound" : BoundingType.UP_TO_SURFACE, "endBoundEntityFace" : qUnion([Q1]), "depth" : 25 * mm});
        }
        {
            var Q0;
            Q0=makeQuery(id+"F3.boolean.opBoolean","COPY",EDGE,{"derivedFrom":makeQuery(id+"F3.opExtrude","CAP_EDGE",EDGE,{"disambiguationData":[OSD([sQuery(id+"F0.wireOp",EDGE,"E25.6")])],"isStart":false})});
            var Q1;
            Q1=makeQuery(id+"F8.boolean.opBoolean","INTERSECT",EDGE,{"derivedFrom":[makeQuery(id+"F5.opExtrude","SWEPT_FACE",FACE,{"disambiguationData":[OSD([sQuery(id+"F4.wireOp",EDGE,"E30")])]}),makeQuery(id+"F8.opExtrude","CAP_FACE",FACE,{"disambiguationData":[OSD([sQuery(id+"F7.wireOp",EDGE,"E67")])],"isStart":false})]});
            var Q2;
            Q2=makeQuery(id+"F8.boolean.opBoolean","INTERSECT",EDGE,{"disambiguationData":[OD(1.0)],"derivedFrom":[makeQuery(id+"F5.opExtrude","SWEPT_FACE",FACE,{"disambiguationData":[OSD([sQuery(id+"F4.wireOp",EDGE,"E30")])]}),makeQuery(id+"F8.opExtrude","SWEPT_FACE",FACE,{"disambiguationData":[OSD([sQuery(id+"F7.wireOp",EDGE,"E67")])]})]});
            var Q3;
            {var subQ0=sQuery(id+"F4.wireOp",EDGE,"E30");Q3=makeQuery(id+"F8.boolean.opBoolean","SPLIT",EDGE,{"disambiguationData":[TD([makeQuery(id+"F5.opExtrude","SWEPT_FACE",FACE,{"disambiguationData":[OSD([sQuery(id+"F4.wireOp",EDGE,"E35.filletArc")])]})])],"derivedFrom":makeQuery(id+"F5.opExtrude","CAP_EDGE",EDGE,{"disambiguationData":[OSD([subQ0])],"isStart":false})});}
            var Q4;
            {var subQ0=sQuery(id+"F0.wireOp",EDGE,"E25.7");var subQ1=sQuery(id+"F0.wireOp",EDGE,"E25.1");var subQ2=sQuery(id+"F0.wireOp",EDGE,"E25.6");var subQ3=sQuery(id+"F0.wireOp",EDGE,"E25.5");var subQ4=sQuery(id+"F0.wireOp",EDGE,"E25.4");var subQ5=sQuery(id+"F0.wireOp",EDGE,"E25.0");var subQ6=sQuery(id+"F0.wireOp",EDGE,"E25.2");var subQ7=sQuery(id+"F0.wireOp",EDGE,"E25.3");Q4=makeQuery(id+"F8.boolean.opBoolean","INTERSECT",EDGE,{"derivedFrom":[makeQuery(id+"F5.boolean.opBoolean","SPLIT",FACE,{"disambiguationData":[TD([makeQuery(id+"F2.opExtrude","SWEPT_FACE",FACE,{"disambiguationData":[OSD([subQ5])]})])],"derivedFrom":makeQuery(id+"F3.boolean.opBoolean","COPY",FACE,{"derivedFrom":makeQuery(id+"F3.opExtrude","CAP_FACE",FACE,{"disambiguationData":[OSD([subQ5,subQ1,subQ6,subQ7,subQ4,subQ3,subQ2,subQ0])],"isStart":false})})}),makeQuery(id+"F8.opExtrude","SWEPT_FACE",FACE,{"disambiguationData":[OSD([sQuery(id+"F7.wireOp",EDGE,"E67")])]})]});}
            var Q5;
            Q5=makeQuery(id+"F8.boolean.opBoolean","INTERSECT",EDGE,{"disambiguationData":[OD(0.0)],"derivedFrom":[makeQuery(id+"F5.opExtrude","SWEPT_FACE",FACE,{"disambiguationData":[OSD([sQuery(id+"F4.wireOp",EDGE,"E30")])]}),makeQuery(id+"F8.opExtrude","SWEPT_FACE",FACE,{"disambiguationData":[OSD([sQuery(id+"F7.wireOp",EDGE,"E67")])]})]});
            fillet(context, id + "F14", {"entities" : qUnion([Q0, Q1, Q2, Q3, Q4, Q5]), "radius" : 3 * mm, "tangentPropagation" : true, "allowEdgeOverflow" : false});
        }
        {
            var Q0;
            Q0=makeQuery(id+"F1.opExtrude","CAP_EDGE",EDGE,{"disambiguationData":[OSD([sQuery(id+"F0.wireOp",EDGE,"E1.bottom")])],"isStart":false});
            fillet(context, id + "F15", {"entities" : qUnion([Q0]), "radius" : 2 * mm, "tangentPropagation" : true, "allowEdgeOverflow" : false});
        }
        {
            var Q0;
            {var subQ0=sQuery(id+"F0.wireOp",EDGE,"E21.filletArc");var subQ1=sQuery(id+"F0.wireOp",EDGE,"E7");var subQ2=sQuery(id+"F0.wireOp",EDGE,"E6");var subQ3=sQuery(id+"F0.wireOp",EDGE,"E5");var subQ4=sQuery(id+"F0.wireOp",EDGE,"E4");var subQ5=sQuery(id+"F0.wireOp",EDGE,"E22.filletArc");var subQ6=sQuery(id+"F0.wireOp",EDGE,"E1.bottom");var subQ7=sQuery(id+"F0.wireOp",EDGE,"E1.right");var subQ8=sQuery(id+"F0.wireOp",EDGE,"E1.top");var subQ9=sQuery(id+"F0.wireOp",EDGE,"E1.left");var subQ10=sQuery(id+"F0.wireOp",EDGE,"E23.filletArc");var subQ11=sQuery(id+"F0.wireOp",EDGE,"E24.filletArc");Q0=makeQuery(id+"F2.boolean.opBoolean","SPLIT",FACE,{"disambiguationData":[TD([makeQuery(id+"F1.opExtrude","SWEPT_FACE",FACE,{"disambiguationData":[OSD([subQ6])]})])],"derivedFrom":makeQuery(id+"F1.opExtrude","CAP_FACE",FACE,{"disambiguationData":[OSD([subQ6,subQ8,subQ9,subQ7,subQ4,subQ3,subQ2,subQ1,subQ0,subQ5,subQ10,subQ11])],"isStart":true})});}
            var sketch = newSketch(context, id + "F16", { "sketchPlane" : qUnion([Q0])});
            skLineSegment(sketch, "E79", {"start": v(-33, 90) * mm, "end": v(-15, 108) * mm});
            skLineSegment(sketch, "E80", {"start": v(33, 90) * mm, "end": v(15, 108) * mm});
            skLineSegment(sketch, "E81", {"start": v(-15, 108) * mm, "end": v(-15, 120) * mm});
            skLineSegment(sketch, "E82", {"start": v(15, 108) * mm, "end": v(15, 120) * mm});
            skLineSegment(sketch, "E83", {"start": v(0, 90) * mm, "end": v(0, 120) * mm, "construction": true});
            skCircle(sketch, "E84", {"center": v(0, 120) * mm, "radius": 6 * mm});
            skLineSegment(sketch, "E85", {"start": v(-80, 0) * mm, "end": v(80, 0) * mm, "construction": true});
            skArc(sketch, "E86", {"start": v(15, 120) * mm, "mid": v(0, 135) * mm, "end": v(-15, 120) * mm});
            skLineSegment(sketch, "E87.MirrorCS", {"start": v(33, -90) * mm, "end": v(15, -108) * mm});
            skLineSegment(sketch, "E88.MirrorCS", {"start": v(15, -108) * mm, "end": v(15, -120) * mm});
            skArc(sketch, "E89.MirrorCS", {"start": v(15, -120) * mm, "mid": v(0, -135) * mm, "end": v(-15, -120) * mm});
            skLineSegment(sketch, "E90.MirrorCS", {"start": v(-15, -108) * mm, "end": v(-15, -120) * mm});
            skLineSegment(sketch, "E91.MirrorCS", {"start": v(-33, -90) * mm, "end": v(-15, -108) * mm});
            skCircle(sketch, "E92.MirrorC", {"center": v(0, -120) * mm, "radius": 6 * mm});
            skLineSegment(sketch, "E93.MirrorCS", {"start": v(0, -90) * mm, "end": v(0, -120) * mm, "construction": true});
            skSolve(sketch);
        }
        {
            var Q0;
            Q0=makeQuery(id+"F16.imprint","IMPRINT",FACE,{"disambiguationData":[TD([[makeQuery(id+"F16.imprint","IMPRINT",EDGE,{"derivedFrom":sQuery(id+"F16.wireOp",EDGE,"b7b7a897-144d-42ed-ab5d-3ee68008480f0.MirrorCS")}),-1.0]])]});
            var Q1;
            Q1=makeQuery(id+"F16.imprint","IMPRINT",FACE,{"disambiguationData":[TD([[makeQuery(id+"F16.imprint","IMPRINT",EDGE,{"derivedFrom":makeQuery(id+"F1.opExtrude","CAP_EDGE",EDGE,{"disambiguationData":[OSD([sQuery(id+"F0.wireOp",EDGE,"E1.left")])],"isStart":true})}),-1.0]])]});
            var Q2;
            {var subQ0=sQuery(id+"F16.wireOp",EDGE,"E79");Q2=makeQuery(id+"F16.imprint","IMPRINT",FACE,{"disambiguationData":[TD([[makeQuery(id+"F16.imprint","IMPRINT",EDGE,{"derivedFrom":subQ0}),-1.0]])]});}
            var Q3;
            {var subQ0=sQuery(id+"F16.wireOp",EDGE,"E87.MirrorCS");Q3=makeQuery(id+"F16.imprint","IMPRINT",FACE,{"disambiguationData":[TD([[makeQuery(id+"F16.imprint","IMPRINT",EDGE,{"derivedFrom":subQ0}),-1.0]])]});}
            var Q4;
            Q4=makeQuery(id+"F2.opExtrude","CAP_FACE",FACE,{"disambiguationData":[OSD([sQuery(id+"F0.wireOp",EDGE,"E12"),sQuery(id+"F0.wireOp",EDGE,"E13"),sQuery(id+"F0.wireOp",EDGE,"E14"),sQuery(id+"F0.wireOp",EDGE,"E15"),sQuery(id+"F0.wireOp",EDGE,"E17.filletArc"),sQuery(id+"F0.wireOp",EDGE,"E18.filletArc"),sQuery(id+"F0.wireOp",EDGE,"E19.filletArc"),sQuery(id+"F0.wireOp",EDGE,"E20.filletArc"),sQuery(id+"F0.wireOp",EDGE,"E25.0"),sQuery(id+"F0.wireOp",EDGE,"E25.1"),sQuery(id+"F0.wireOp",EDGE,"E25.2"),sQuery(id+"F0.wireOp",EDGE,"E25.3"),sQuery(id+"F0.wireOp",EDGE,"E25.4"),sQuery(id+"F0.wireOp",EDGE,"E25.5"),sQuery(id+"F0.wireOp",EDGE,"E25.6"),sQuery(id+"F0.wireOp",EDGE,"E25.7")])],"isStart":false});
            extrude(context, id + "F17", {"entities" : qUnion([Q0, Q1, Q2, Q3]), "operationType" : NewBodyOperationType.ADD, "endBound" : BoundingType.UP_TO_SURFACE, "endBoundEntityFace" : qUnion([Q4]), "depth" : 25 * mm});
        }
    });
